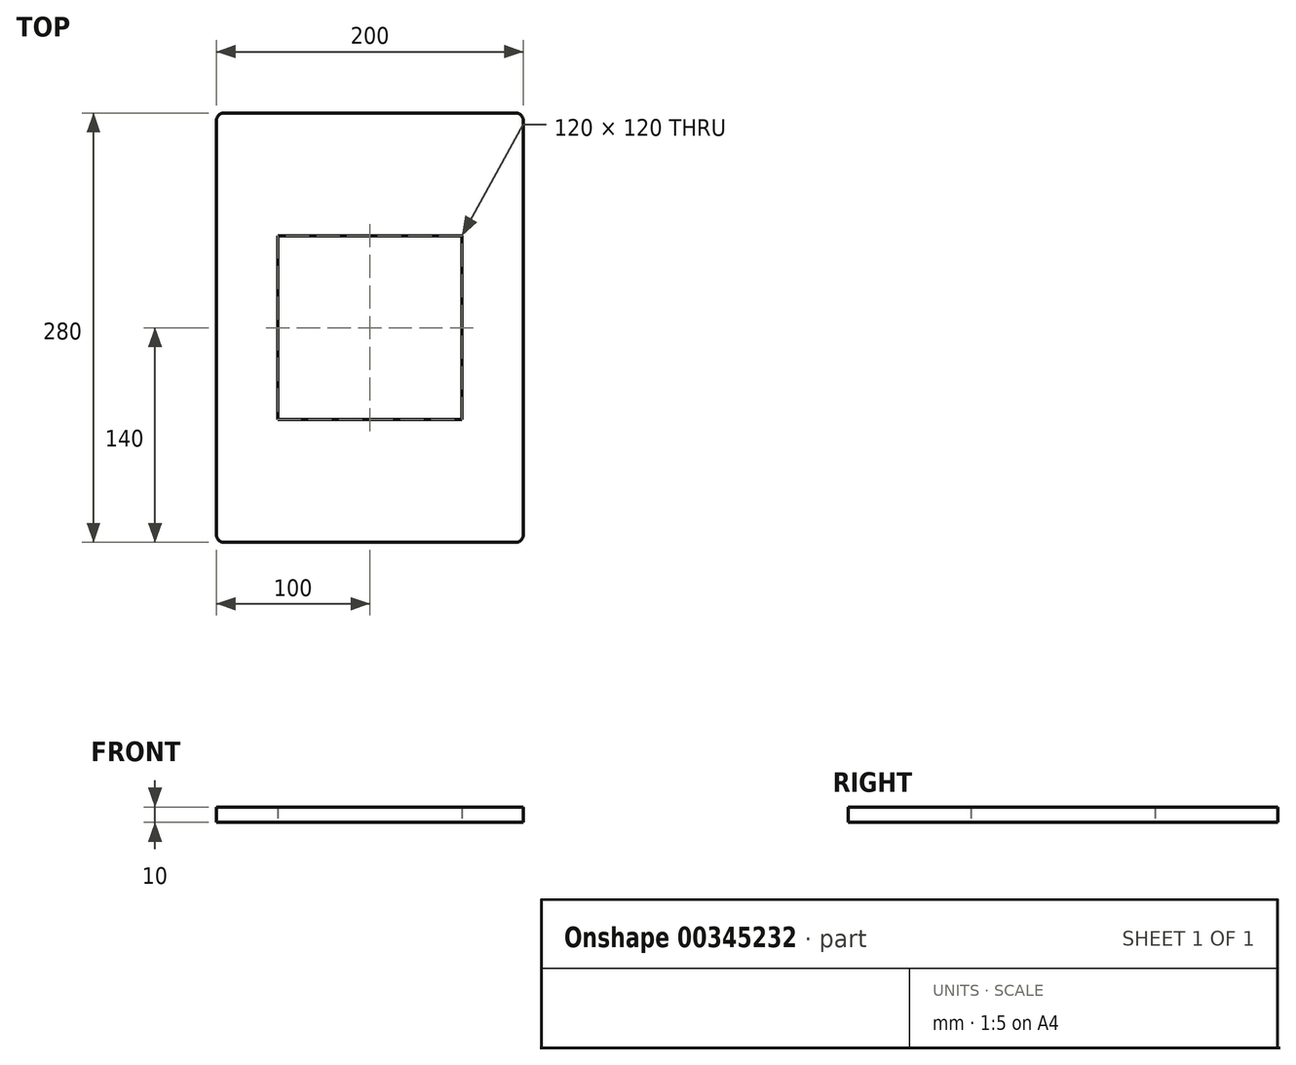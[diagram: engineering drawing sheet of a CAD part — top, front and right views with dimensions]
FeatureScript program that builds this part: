
annotation { "Feature Type Name" : "Feature", "Feature Type Description" : "" }
export const myFeature = defineFeature(function(context is Context, id is Id, definition is map)
    precondition{}
    {
        {
            var Q0;
            Q0=qCreatedBy(makeId("Top.planeOp"),FACE);
            var sketch = newSketch(context, id + "F0", { "sketchPlane" : qUnion([Q0])});
            skLineSegment(sketch, "E0.bottom", {"start": v(-95, 140) * mm, "end": v(95, 140) * mm});
            skLineSegment(sketch, "E0.top", {"start": v(-95, -140) * mm, "end": v(95, -140) * mm});
            skLineSegment(sketch, "E0.left", {"start": v(-100, 135) * mm, "end": v(-100, -135) * mm});
            skLineSegment(sketch, "E0.right", {"start": v(100, 135) * mm, "end": v(100, -135) * mm});
            skPoint(sketch, "E0.middle", {"position": v(0, 0) * mm});
            skLineSegment(sketch, "E1.bottom", {"start": v(-60, 60) * mm, "end": v(60, 60) * mm});
            skLineSegment(sketch, "E1.top", {"start": v(-60, -60) * mm, "end": v(60, -60) * mm});
            skLineSegment(sketch, "E1.left", {"start": v(-60, 60) * mm, "end": v(-60, -60) * mm});
            skLineSegment(sketch, "E1.right", {"start": v(60, 60) * mm, "end": v(60, -60) * mm});
            skPoint(sketch, "E2.visualSharp", {"position": v(-100, 140) * mm});
            skArc(sketch, "E2.filletArc", {"start": v(-95, 140) * mm, "mid": v(-98.54, 138.54) * mm, "end": v(-100, 135) * mm});
            skPoint(sketch, "E3.visualSharp", {"position": v(100, 140) * mm});
            skArc(sketch, "E3.filletArc", {"start": v(100, 135) * mm, "mid": v(98.54, 138.54) * mm, "end": v(95, 140) * mm});
            skPoint(sketch, "E4.visualSharp", {"position": v(100, -140) * mm});
            skArc(sketch, "E4.filletArc", {"start": v(95, -140) * mm, "mid": v(98.54, -138.54) * mm, "end": v(100, -135) * mm});
            skPoint(sketch, "E5.visualSharp", {"position": v(-100, -140) * mm});
            skArc(sketch, "E5.filletArc", {"start": v(-100, -135) * mm, "mid": v(-98.54, -138.54) * mm, "end": v(-95, -140) * mm});
            skSolve(sketch);
        }
        {
            var Q0;
            Q0=qSketchRegion(id+"F0",true);
            extrude(context, id + "F1", {"entities" : qUnion([Q0]), "depth" : 10 * mm});
        }
    });
